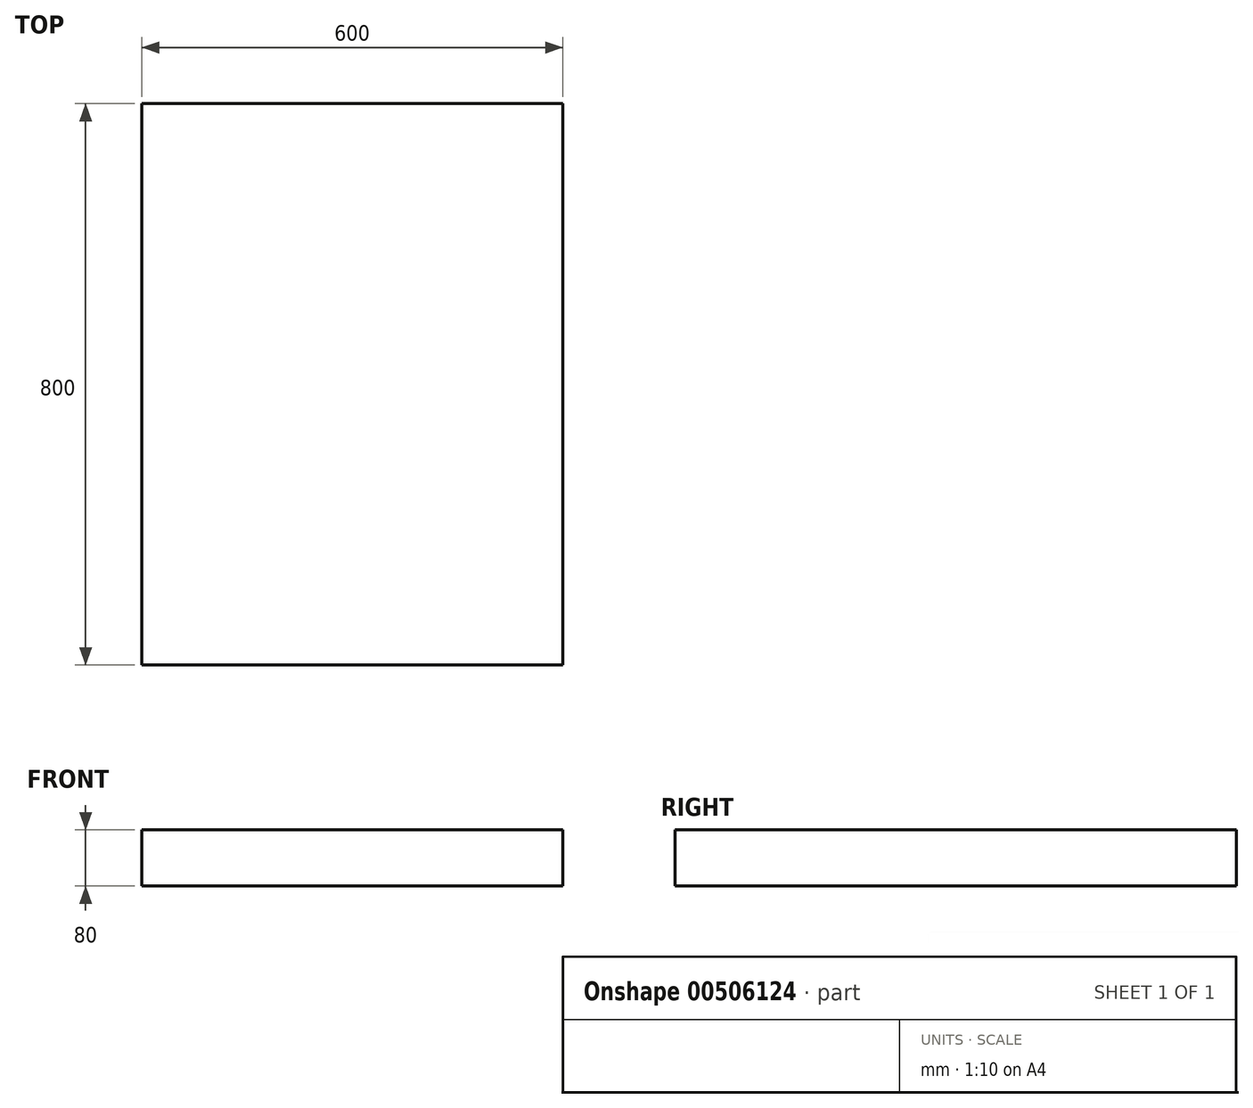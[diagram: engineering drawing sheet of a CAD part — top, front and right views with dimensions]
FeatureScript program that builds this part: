
annotation { "Feature Type Name" : "Feature", "Feature Type Description" : "" }
export const myFeature = defineFeature(function(context is Context, id is Id, definition is map)
    precondition{}
    {
        {
            var Q0;
            Q0=qCreatedBy(makeId("Top.planeOp"),FACE);
            var sketch = newSketch(context, id + "F0", { "sketchPlane" : qUnion([Q0])});
            skLineSegment(sketch, "E0.bottom", {"start": v(300, -400) * mm, "end": v(-300, -400) * mm});
            skLineSegment(sketch, "E0.top", {"start": v(300, 400) * mm, "end": v(-300, 400) * mm});
            skLineSegment(sketch, "E0.left", {"start": v(300, -400) * mm, "end": v(300, 400) * mm});
            skLineSegment(sketch, "E0.right", {"start": v(-300, -400) * mm, "end": v(-300, 400) * mm});
            skPoint(sketch, "E0.middle", {"position": v(0, 0) * mm});
            skSolve(sketch);
        }
        {
            var Q0;
            Q0 = qSketchRegion(id + "F0", true);
            extrude(context, id + "F1", {"entities" : qUnion([Q0]), "depth" : 80 * mm});
        }
    });
